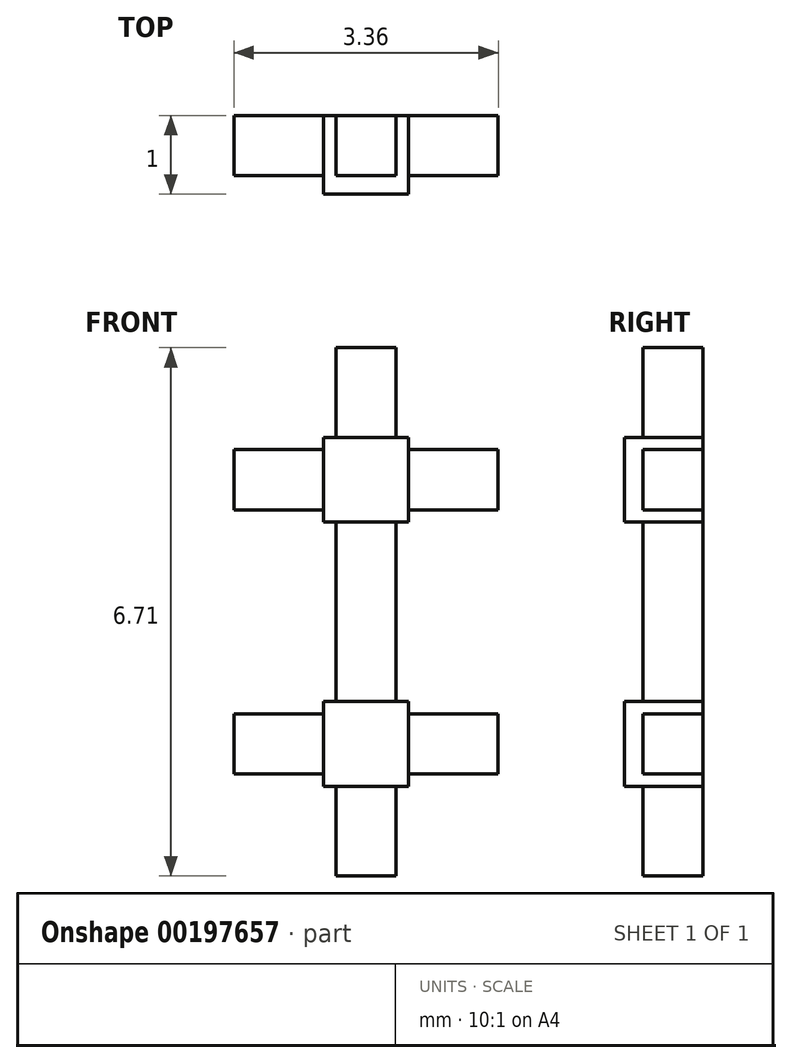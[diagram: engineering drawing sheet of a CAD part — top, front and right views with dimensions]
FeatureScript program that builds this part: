
annotation { "Feature Type Name" : "Feature", "Feature Type Description" : "" }
export const myFeature = defineFeature(function(context is Context, id is Id, definition is map)
    precondition{}
    {
        {
            var Q0;
            Q0=qCreatedBy(makeId("Front.planeOp"),FACE);
            var sketch = newSketch(context, id + "F0", { "sketchPlane" : qUnion([Q0])});
            skLineSegment(sketch, "E0.bottom", {"start": v(0.54, 0.54) * mm, "end": v(-0.54, 0.54) * mm});
            skLineSegment(sketch, "E0.top", {"start": v(0.54, -0.54) * mm, "end": v(-0.54, -0.54) * mm});
            skLineSegment(sketch, "E0.left", {"start": v(0.54, 0.54) * mm, "end": v(0.54, -0.54) * mm});
            skLineSegment(sketch, "E0.right", {"start": v(-0.54, 0.54) * mm, "end": v(-0.54, -0.54) * mm});
            skPoint(sketch, "E0.middle", {"position": v(0, 0) * mm});
            skSolve(sketch);
        }
        {
            var Q0;
            Q0 = qSketchRegion(id + "F0", true);
            extrude(context, id + "F1", {"entities" : qUnion([Q0]), "depth" : 1 * mm});
        }
        {
            var Q0;
            Q0=makeQuery(id+"F1.opExtrude","SWEPT_FACE",FACE,{"disambiguationData":[OSD([sQuery(id+"F0.wireOp",EDGE,"E0.top")])]});
            var sketch = newSketch(context, id + "F2", { "sketchPlane" : qUnion([Q0])});
            skLineSegment(sketch, "E1", {"start": v(-0.54, 0) * mm, "end": v(-0.38, 0) * mm});
            skLineSegment(sketch, "E2", {"start": v(0.54, 0) * mm, "end": v(0.38, 0) * mm});
            skLineSegment(sketch, "E3.bottom", {"start": v(-0.38, 0) * mm, "end": v(0.38, 0) * mm});
            skLineSegment(sketch, "E3.top", {"start": v(-0.38, 0.76) * mm, "end": v(0.38, 0.76) * mm});
            skLineSegment(sketch, "E3.left", {"start": v(-0.38, 0) * mm, "end": v(-0.38, 0.76) * mm});
            skLineSegment(sketch, "E3.right", {"start": v(0.38, 0) * mm, "end": v(0.38, 0.76) * mm});
            skSolve(sketch);
        }
        {
            var Q0;
            Q0 = qSketchRegion(id + "F2", true);
            extrude(context, id + "F3", {"entities" : qUnion([Q0]), "operationType" : NewBodyOperationType.ADD, "depth" : 1.14 * mm});
        }
        {
            var Q0;
            Q0=makeQuery(id+"F1.opExtrude","SWEPT_FACE",FACE,{"disambiguationData":[OSD([sQuery(id+"F0.wireOp",EDGE,"E0.right")])]});
            var sketch = newSketch(context, id + "F4", { "sketchPlane" : qUnion([Q0])});
            skLineSegment(sketch, "E4", {"start": v(0, -0.54) * mm, "end": v(0, -0.38) * mm});
            skLineSegment(sketch, "E5.bottom", {"start": v(0, -0.38) * mm, "end": v(0.76, -0.38) * mm});
            skLineSegment(sketch, "E5.top", {"start": v(0, 0.38) * mm, "end": v(0.76, 0.38) * mm});
            skLineSegment(sketch, "E5.left", {"start": v(0, -0.38) * mm, "end": v(0, 0.38) * mm});
            skLineSegment(sketch, "E5.right", {"start": v(0.76, -0.38) * mm, "end": v(0.76, 0.38) * mm});
            skSolve(sketch);
        }
        {
            var Q0;
            Q0 = qSketchRegion(id + "F4", true);
            extrude(context, id + "F5", {"entities" : qUnion([Q0]), "operationType" : NewBodyOperationType.ADD, "depth" : 1.14 * mm});
        }
        {
            var Q0;
            Q0=makeQuery(id+"F1.opExtrude","SWEPT_FACE",FACE,{"disambiguationData":[OSD([sQuery(id+"F0.wireOp",EDGE,"E0.left")])]});
            var sketch = newSketch(context, id + "F6", { "sketchPlane" : qUnion([Q0])});
            skLineSegment(sketch, "E6", {"start": v(0, 0.54) * mm, "end": v(0, 0.38) * mm});
            skLineSegment(sketch, "E7.bottom", {"start": v(0, 0.38) * mm, "end": v(-0.76, 0.38) * mm});
            skLineSegment(sketch, "E7.top", {"start": v(0, -0.38) * mm, "end": v(-0.76, -0.38) * mm});
            skLineSegment(sketch, "E7.left", {"start": v(0, 0.38) * mm, "end": v(0, -0.38) * mm});
            skLineSegment(sketch, "E7.right", {"start": v(-0.76, 0.38) * mm, "end": v(-0.76, -0.38) * mm});
            skSolve(sketch);
        }
        {
            var Q0;
            Q0 = qSketchRegion(id + "F6", true);
            extrude(context, id + "F7", {"entities" : qUnion([Q0]), "operationType" : NewBodyOperationType.ADD, "depth" : 1.14 * mm});
        }
        {
            var Q0;
            Q0=makeQuery(id+"F1.opExtrude","SWEPT_FACE",FACE,{"disambiguationData":[OSD([sQuery(id+"F0.wireOp",EDGE,"E0.bottom")])]});
            var sketch = newSketch(context, id + "F8", { "sketchPlane" : qUnion([Q0])});
            skLineSegment(sketch, "E8", {"start": v(0.54, 0) * mm, "end": v(0.38, 0) * mm});
            skLineSegment(sketch, "E9.bottom", {"start": v(0.38, 0) * mm, "end": v(-0.38, 0) * mm});
            skLineSegment(sketch, "E9.top", {"start": v(0.38, -0.76) * mm, "end": v(-0.38, -0.76) * mm});
            skLineSegment(sketch, "E9.left", {"start": v(0.38, 0) * mm, "end": v(0.38, -0.76) * mm});
            skLineSegment(sketch, "E9.right", {"start": v(-0.38, 0) * mm, "end": v(-0.38, -0.76) * mm});
            skSolve(sketch);
        }
        {
            var Q0;
            Q0 = qSketchRegion(id + "F8", true);
            extrude(context, id + "F9", {"entities" : qUnion([Q0]), "operationType" : NewBodyOperationType.ADD, "depth" : 2.27 * mm});
        }
        {
            var Q0;
            Q0=makeQuery(id+"F9.opExtrude","CAP_FACE",FACE,{"disambiguationData":[OSD([sQuery(id+"F8.wireOp",EDGE,"E9.bottom"),sQuery(id+"F8.wireOp",EDGE,"E9.top"),sQuery(id+"F8.wireOp",EDGE,"E9.left"),sQuery(id+"F8.wireOp",EDGE,"E9.right")])],"isStart":false});
            var sketch = newSketch(context, id + "F10", { "sketchPlane" : qUnion([Q0])});
            skLineSegment(sketch, "E10", {"start": v(0.38, 0) * mm, "end": v(0.54, 0) * mm});
            skLineSegment(sketch, "E11.bottom", {"start": v(0.54, 0) * mm, "end": v(-0.54, 0) * mm});
            skLineSegment(sketch, "E11.top", {"start": v(0.54, -1) * mm, "end": v(-0.54, -1) * mm});
            skLineSegment(sketch, "E11.left", {"start": v(0.54, 0) * mm, "end": v(0.54, -1) * mm});
            skLineSegment(sketch, "E11.right", {"start": v(-0.54, 0) * mm, "end": v(-0.54, -1) * mm});
            skSolve(sketch);
        }
        {
            var Q0;
            Q0 = qSketchRegion(id + "F10", true);
            extrude(context, id + "F11", {"entities" : qUnion([Q0]), "operationType" : NewBodyOperationType.ADD, "depth" : 1.08 * mm});
        }
        {
            var Q0;
            Q0=makeQuery(id+"F11.opExtrude","SWEPT_FACE",FACE,{"disambiguationData":[OSD([sQuery(id+"F10.wireOp",EDGE,"E11.left")])]});
            var sketch = newSketch(context, id + "F12", { "sketchPlane" : qUnion([Q0])});
            skLineSegment(sketch, "E12", {"start": v(0, 2.81) * mm, "end": v(0, 2.97) * mm});
            skLineSegment(sketch, "E13.bottom", {"start": v(0, 2.97) * mm, "end": v(-0.76, 2.97) * mm});
            skLineSegment(sketch, "E13.top", {"start": v(0, 3.73) * mm, "end": v(-0.76, 3.73) * mm});
            skLineSegment(sketch, "E13.left", {"start": v(0, 2.97) * mm, "end": v(0, 3.73) * mm});
            skLineSegment(sketch, "E13.right", {"start": v(-0.76, 2.97) * mm, "end": v(-0.76, 3.73) * mm});
            skSolve(sketch);
        }
        {
            var Q0;
            Q0 = qSketchRegion(id + "F12", true);
            extrude(context, id + "F13", {"entities" : qUnion([Q0]), "operationType" : NewBodyOperationType.ADD, "depth" : 1.14 * mm});
        }
        {
            var Q0;
            Q0=makeQuery(id+"F11.opExtrude","CAP_FACE",FACE,{"disambiguationData":[OSD([sQuery(id+"F10.wireOp",EDGE,"E11.bottom"),sQuery(id+"F10.wireOp",EDGE,"E11.top"),sQuery(id+"F10.wireOp",EDGE,"E11.left"),sQuery(id+"F10.wireOp",EDGE,"E11.right")])],"isStart":false});
            var sketch = newSketch(context, id + "F14", { "sketchPlane" : qUnion([Q0])});
            skLineSegment(sketch, "E14", {"start": v(0.54, 0) * mm, "end": v(0.38, 0) * mm});
            skLineSegment(sketch, "E15.bottom", {"start": v(0.38, 0) * mm, "end": v(-0.38, 0) * mm});
            skLineSegment(sketch, "E15.top", {"start": v(0.38, -0.76) * mm, "end": v(-0.38, -0.76) * mm});
            skLineSegment(sketch, "E15.left", {"start": v(0.38, 0) * mm, "end": v(0.38, -0.76) * mm});
            skLineSegment(sketch, "E15.right", {"start": v(-0.38, 0) * mm, "end": v(-0.38, -0.76) * mm});
            skSolve(sketch);
        }
        {
            var Q0;
            Q0 = qSketchRegion(id + "F14", true);
            extrude(context, id + "F15", {"entities" : qUnion([Q0]), "operationType" : NewBodyOperationType.ADD, "depth" : 1.14 * mm});
        }
        {
            var Q0;
            Q0=makeQuery(id+"F11.opExtrude","SWEPT_FACE",FACE,{"disambiguationData":[OSD([sQuery(id+"F10.wireOp",EDGE,"E11.right")])]});
            var sketch = newSketch(context, id + "F16", { "sketchPlane" : qUnion([Q0])});
            skLineSegment(sketch, "E16", {"start": v(0, 3.9) * mm, "end": v(0, 3.73) * mm});
            skLineSegment(sketch, "E17.bottom", {"start": v(0, 3.73) * mm, "end": v(0.76, 3.73) * mm});
            skLineSegment(sketch, "E17.top", {"start": v(0, 2.97) * mm, "end": v(0.76, 2.97) * mm});
            skLineSegment(sketch, "E17.left", {"start": v(0, 3.73) * mm, "end": v(0, 2.97) * mm});
            skLineSegment(sketch, "E17.right", {"start": v(0.76, 3.73) * mm, "end": v(0.76, 2.97) * mm});
            skSolve(sketch);
        }
        {
            var Q0;
            Q0 = qSketchRegion(id + "F16", true);
            extrude(context, id + "F17", {"entities" : qUnion([Q0]), "operationType" : NewBodyOperationType.ADD, "depth" : 1.14 * mm});
        }
    });
